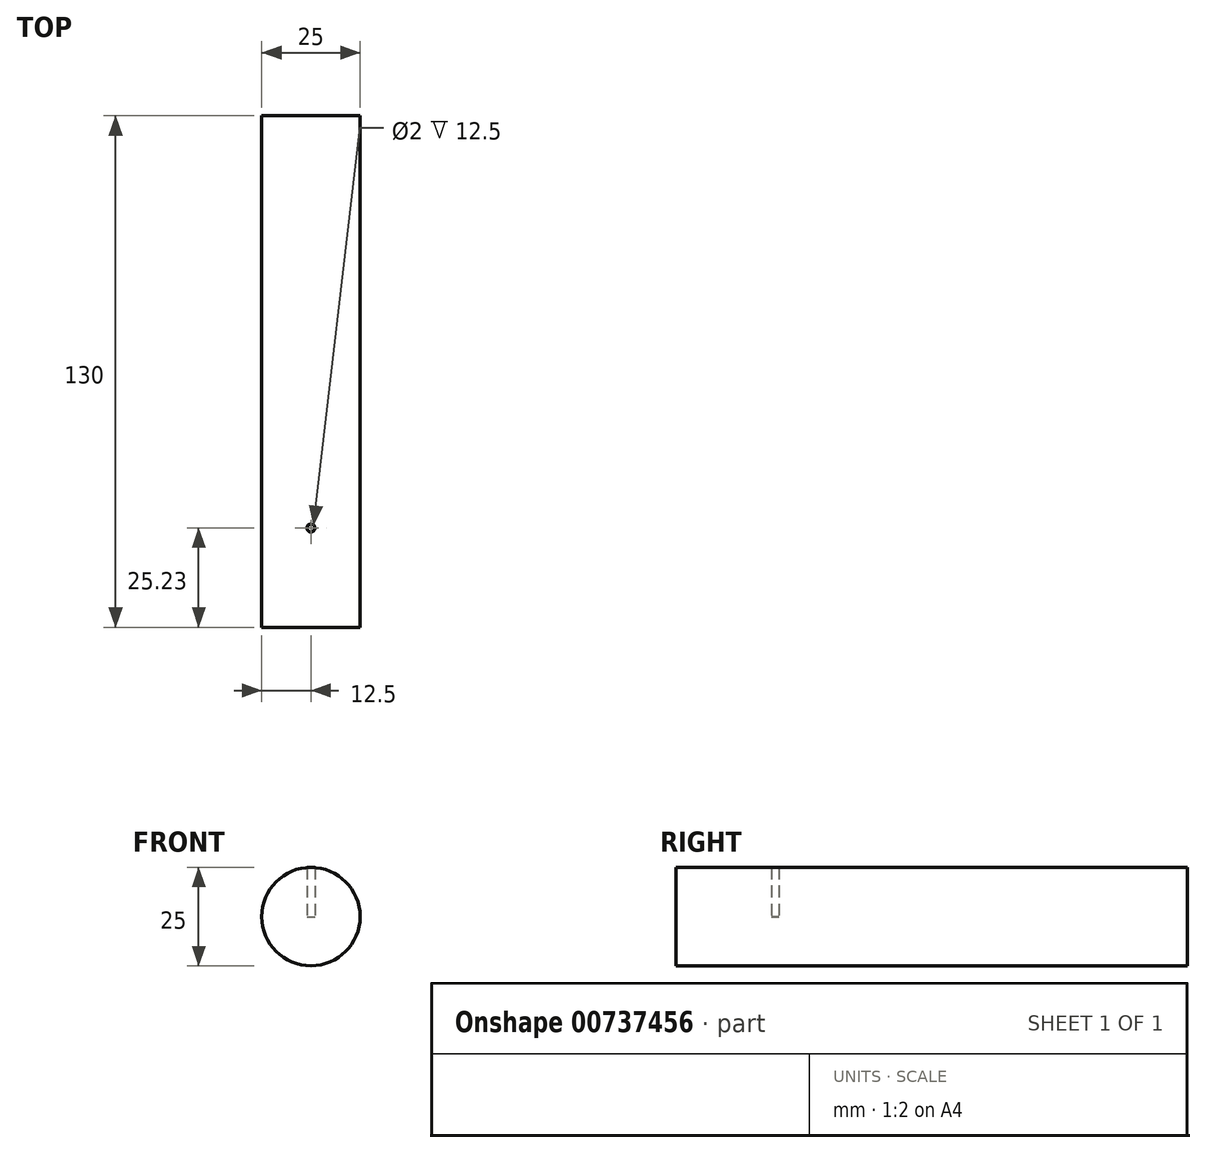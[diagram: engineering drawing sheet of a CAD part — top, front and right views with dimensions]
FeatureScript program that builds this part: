
annotation { "Feature Type Name" : "Feature", "Feature Type Description" : "" }
export const myFeature = defineFeature(function(context is Context, id is Id, definition is map)
    precondition{}
    {
        {
            var Q0;
            Q0=qCreatedBy(makeId("Front.planeOp"),FACE);
            var sketch = newSketch(context, id + "F0", { "sketchPlane" : qUnion([Q0])});
            skCircle(sketch, "E0", {"center": v(0, 0) * mm, "radius": 12.5 * mm});
            skSolve(sketch);
        }
        {
            var Q0;
            Q0=makeQuery(id+"F0.imprint","IMPRINT",FACE,{"disambiguationData":[TD([[makeQuery(id+"F0.imprint","IMPRINT",EDGE,{"derivedFrom":sQuery(id+"F0.wireOp",EDGE,"E0")}),1.0]])]});
            extrude(context, id + "F1", {"entities" : qUnion([Q0]), "depth" : 130 * mm, "offsetDistance" : 25 * mm});
        }
        {
            var Q0;
            Q0=qCreatedBy(makeId("Top.planeOp"),FACE);
            var sketch = newSketch(context, id + "F2", { "sketchPlane" : qUnion([Q0])});
            skCircle(sketch, "E1", {"center": v(0, -104.77) * mm, "radius": 2.5 * mm});
            skSolve(sketch);
        }
        {
            var Q0;
            Q0=sQuery(id+"F2.wireOp",VERTEX,"E1.center");
            var Q1;
            Q1=makeQuery(id+"F1.opExtrude","SWEPT_BODY",BODY,{"disambiguationData":[OSD([sQuery(id+"F0.wireOp",EDGE,"E0")])]});
            hole(context, id + "F3", {"style" : HoleStyle.SIMPLE, "endStyle" : HoleEndStyle.THROUGH, "oppositeDirection" : true, "holeDiameter" : 2 * mm, "majorDiameter" : 5 * mm, "isTappedThrough" : true, "tappedDepth" : 12 * mm, "tapClearance" : 3, "locations" : qUnion([Q0]), "scope" : qUnion([Q1])});
        }
    });
